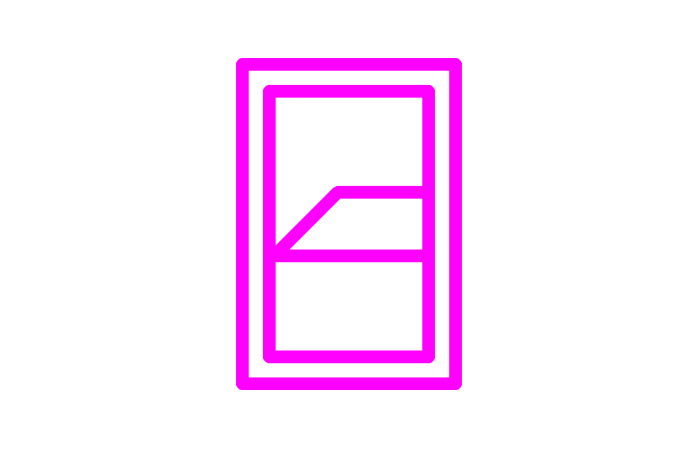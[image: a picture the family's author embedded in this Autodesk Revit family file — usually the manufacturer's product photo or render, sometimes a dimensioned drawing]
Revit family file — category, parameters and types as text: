
# Revit family: Считыватель AGRG SH-I_на гарни
name_source: partatom
category: Охранная сигнализация
units: mm (PartAtom-declared; Revit-internal decimal feet)

## family parameters
Общий = Нет
Основа = Грань
При загрузке вырезать с полостями = Нет
Размер круглого соединителя = Использовать диаметр
Сохранять ориентацию аннотаций = Нет
Тип детали = Нормальный
Точка расчета площади = Нет

## types (1)
- Считыватель AGRG SH-I_на гарни
    ADSK_Верхний порог напряжения = 15 В
    ADSK_Группирование = 1. Оборудование
    ADSK_Единица измерения = шт.
    ADSK_Завод-изготовитель = ООО «Агрегатор»
    ADSK_Код изделия = ESCTLSHI
    ADSK_Количество = 1
    ADSK_Марка = AGRG ЦОД
    ADSK_Масса = 0.55
    ADSK_Наименование = Ручка AGRG SH-I с электронным замком и встроенным мультиформатным считывателем карт для защиты и контроля доступа к телекоммуникационным и другим шкафам. Поддерживаемый тип карт: MIFARE (UID);Mifare Mini, Mifare Classic, Mifare Plus SL1/SL3,Mifare DESFire (UID и чтение из защищеннойьобласти карты); Mifare ID (UID и чтение из защищенных секторов карты).Только карты пользователей (не карты программирования и инициализации);I-CODE (ISO15693) (UID);EM-Marine (UID);HID 125 кГц (UID);Indala (Motorola) (UID);NFC (при установке приложения на смартфон,только ОС Android). Интерфейсы: W-26,34,37,40,42,58, TM (DS1990A);в секторном режиме до W-64. Цвет черный. Работает с различными системами контроля и управления доступом.
    ADSK_Наименование краткое = Ручка с электронным замком и встроенным мультиформатным считывателем карт
    ADSK_Нижний порог напряжения = 9 В
    ADSK_Обозначение = RC
    ITV_SUB_УГО на структурной схеме = УГО_Считыватель с защелкой
    URL = https://skud.agrg.ru
    Изображение типоразмера = RC_castle.png
    Материал = Пластмасса, непрозрачная, черная
    Описание = ITV
    Отметка по умолчанию = 1219 мм
